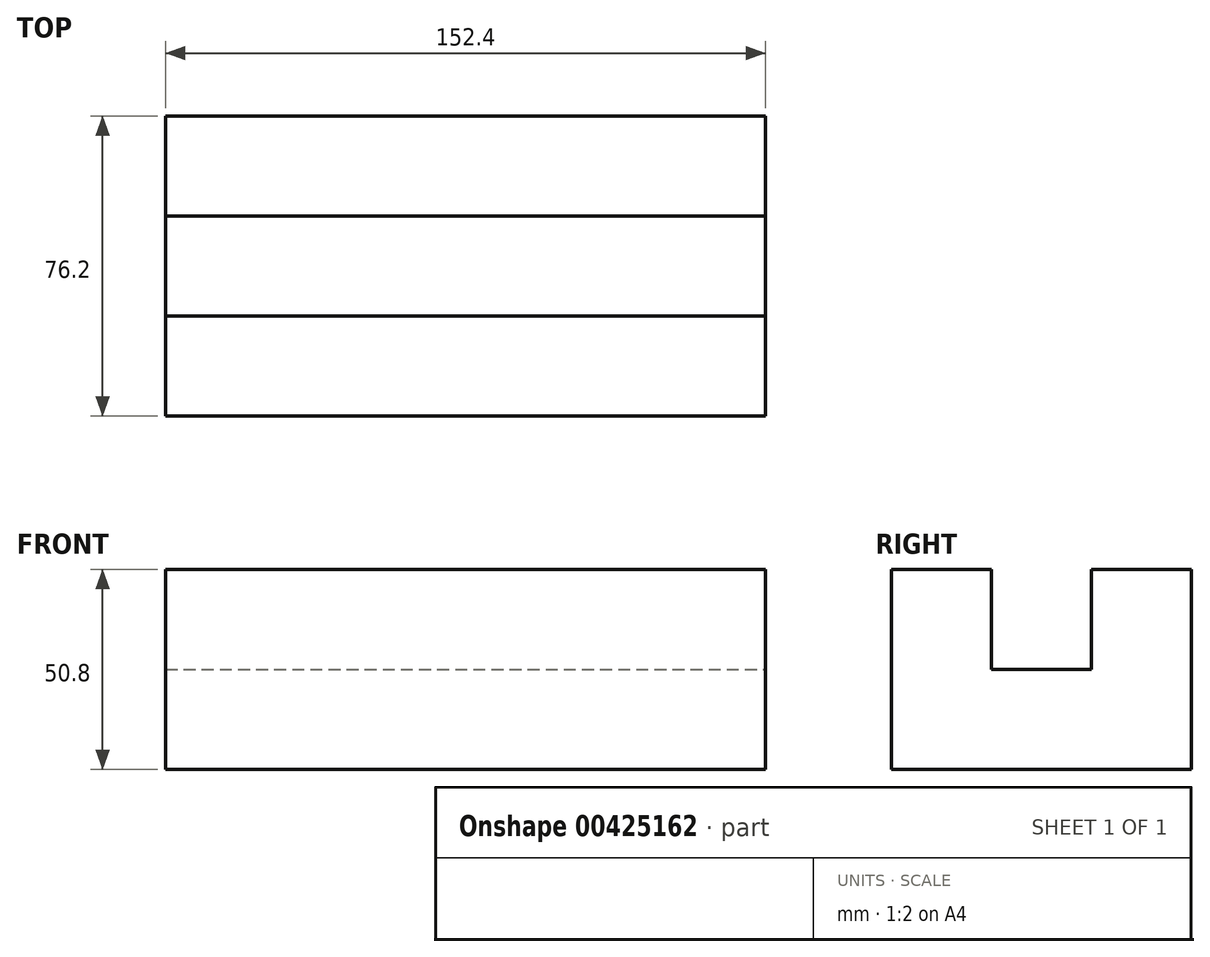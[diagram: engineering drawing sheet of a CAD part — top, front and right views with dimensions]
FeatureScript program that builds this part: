
annotation { "Feature Type Name" : "Feature", "Feature Type Description" : "" }
export const myFeature = defineFeature(function(context is Context, id is Id, definition is map)
    precondition{}
    {
        {
            var Q0;
            Q0=qCreatedBy(makeId("Front.planeOp"),FACE);
            var sketch = newSketch(context, id + "F0", { "sketchPlane" : qUnion([Q0])});
            skLineSegment(sketch, "E0", {"start": v(0, 0) * mm, "end": v(152.4, 0) * mm});
            skLineSegment(sketch, "E1", {"start": v(152.4, 0) * mm, "end": v(152.4, 50.8) * mm});
            skLineSegment(sketch, "E2", {"start": v(152.4, 50.8) * mm, "end": v(0, 50.8) * mm});
            skLineSegment(sketch, "E3", {"start": v(0, 50.8) * mm, "end": v(0, -2.3) * mm});
            skSolve(sketch);
        }
        {
            var Q0;
            {var subQ0=sQuery(id+"F0.wireOp",EDGE,"E0");Q0=makeQuery(id+"F0.imprint","IMPRINT",FACE,{"disambiguationData":[TD([[makeQuery(id+"F0.imprint","IMPRINT",EDGE,{"derivedFrom":subQ0}),1.0]])]});}
            extrude(context, id + "F1", {"entities" : qUnion([Q0]), "depth" : 76.2 * mm});
        }
        {
            var Q0;
            Q0=makeQuery(id+"F1.opExtrude","SWEPT_FACE",FACE,{"disambiguationData":[OSD([sQuery(id+"F0.wireOp",EDGE,"E1")])]});
            var sketch = newSketch(context, id + "F2", { "sketchPlane" : qUnion([Q0])});
            skLineSegment(sketch, "E4", {"start": v(0, 50.8) * mm, "end": v(-25.4, 50.8) * mm});
            skLineSegment(sketch, "E5", {"start": v(-25.4, 50.8) * mm, "end": v(-50.8, 50.8) * mm});
            skLineSegment(sketch, "E6", {"start": v(-50.8, 50.8) * mm, "end": v(-50.8, 25.4) * mm});
            skLineSegment(sketch, "E7", {"start": v(-50.8, 25.4) * mm, "end": v(-25.4, 25.4) * mm});
            skLineSegment(sketch, "E8", {"start": v(-25.4, 25.4) * mm, "end": v(-25.4, 50.8) * mm});
            skSolve(sketch);
        }
        {
            var Q0;
            Q0=makeQuery(id+"F2.imprint","IMPRINT",FACE,{"disambiguationData":[TD([[makeQuery(id+"F2.imprint","IMPRINT",EDGE,{"derivedFrom":sQuery(id+"F2.wireOp",EDGE,"E5")}),-1.0]])]});
            extrude(context, id + "F3", {"entities" : qUnion([Q0]), "operationType" : NewBodyOperationType.REMOVE, "oppositeDirection" : true, "depth" : 152.4 * mm});
        }
    });
